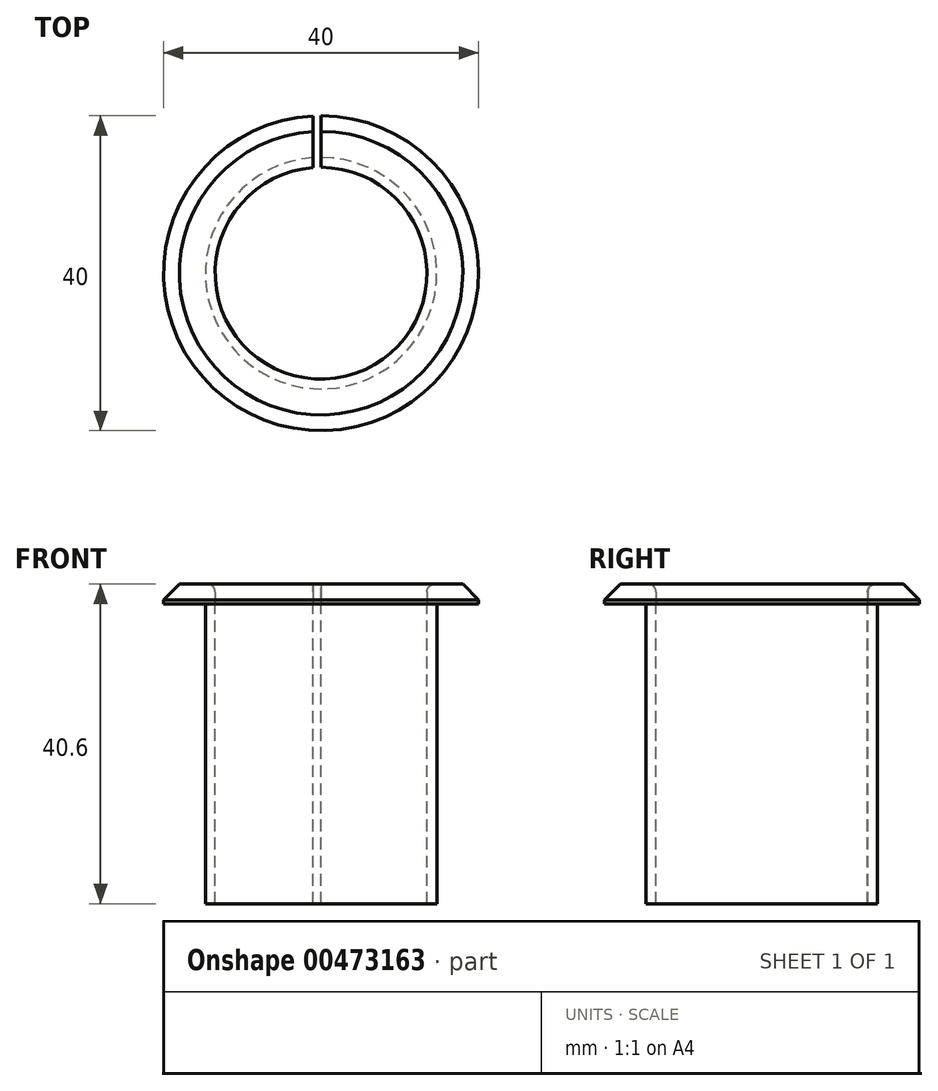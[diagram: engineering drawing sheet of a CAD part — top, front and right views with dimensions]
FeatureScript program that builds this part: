
annotation { "Feature Type Name" : "Feature", "Feature Type Description" : "" }
export const myFeature = defineFeature(function(context is Context, id is Id, definition is map)
    precondition{}
    {
        {
            var Q0;
            Q0=qCreatedBy(makeId("Top.planeOp"),FACE);
            var sketch = newSketch(context, id + "F0", { "sketchPlane" : qUnion([Q0])});
            skCircle(sketch, "E0", {"center": v(0, 0) * mm, "radius": 13.45 * mm});
            skCircle(sketch, "E1", {"center": v(0, 0) * mm, "radius": 20 * mm});
            skCircle(sketch, "E2", {"center": v(0, 0) * mm, "radius": 14.7 * mm});
            skSolve(sketch);
        }
        {
            var Q0;
            Q0=makeQuery(id+"F0.imprint","IMPRINT",FACE,{"disambiguationData":[TD([[makeQuery(id+"F0.imprint","IMPRINT",EDGE,{"derivedFrom":sQuery(id+"F0.wireOp",EDGE,"E0")}),-1.0]])]});
            extrude(context, id + "F1", {"entities" : qUnion([Q0]), "oppositeDirection" : true, "depth" : 38.1 * mm});
        }
        {
            var Q0;
            Q0=makeQuery(id+"F0.imprint","IMPRINT",FACE,{"disambiguationData":[TD([[makeQuery(id+"F0.imprint","IMPRINT",EDGE,{"derivedFrom":sQuery(id+"F0.wireOp",EDGE,"E0")}),-1.0]])]});
            var Q1;
            Q1=makeQuery(id+"F0.imprint","IMPRINT",FACE,{"disambiguationData":[TD([[makeQuery(id+"F0.imprint","IMPRINT",EDGE,{"derivedFrom":sQuery(id+"F0.wireOp",EDGE,"E1")}),1.0]])]});
            extrude(context, id + "F2", {"entities" : qUnion([Q0, Q1]), "depth" : 2.5 * mm});
        }
        {
            var Q0;
            Q0=makeQuery(id+"F2.opExtrude","CAP_EDGE",EDGE,{"disambiguationData":[OSD([sQuery(id+"F0.wireOp",EDGE,"E1")])],"isStart":false});
            chamfer(context, id + "F3", {"entities" : qUnion([Q0]), "width" : 2 * mm, "tangentPropagation" : true});
        }
        {
            var Q0;
            Q0=makeQuery(id+"F2.opExtrude","CAP_EDGE",EDGE,{"disambiguationData":[OSD([sQuery(id+"F0.wireOp",EDGE,"E0")])],"isStart":false});
            fillet(context, id + "F4", {"entities" : qUnion([Q0]), "radius" : 1 * mm, "tangentPropagation" : true, "allowEdgeOverflow" : false});
        }
        {
            var Q0;
            Q0=qCreatedBy(makeId("Right.planeOp"),FACE);
            var sketch = newSketch(context, id + "F5", { "sketchPlane" : qUnion([Q0])});
            skLineSegment(sketch, "E3.bottom", {"start": v(0, 10.57) * mm, "end": v(26.7, 10.57) * mm});
            skLineSegment(sketch, "E3.top", {"start": v(0, -45.57) * mm, "end": v(26.7, -45.57) * mm});
            skLineSegment(sketch, "E3.left", {"start": v(0, 10.57) * mm, "end": v(0, -45.57) * mm});
            skLineSegment(sketch, "E3.right", {"start": v(26.7, 10.57) * mm, "end": v(26.7, -45.57) * mm});
            skSolve(sketch);
        }
        {
            var Q0;
            Q0=makeQuery(id+"F5.imprint","IMPRINT",FACE,{"disambiguationData":[TD([[makeQuery(id+"F5.imprint","IMPRINT",EDGE,{"derivedFrom":sQuery(id+"F5.wireOp",EDGE,"E3.bottom")}),-1.0]])]});
            extrude(context, id + "F6", {"entities" : qUnion([Q0]), "operationType" : NewBodyOperationType.REMOVE, "oppositeDirection" : true, "depth" : 1 * mm});
        }
    });
